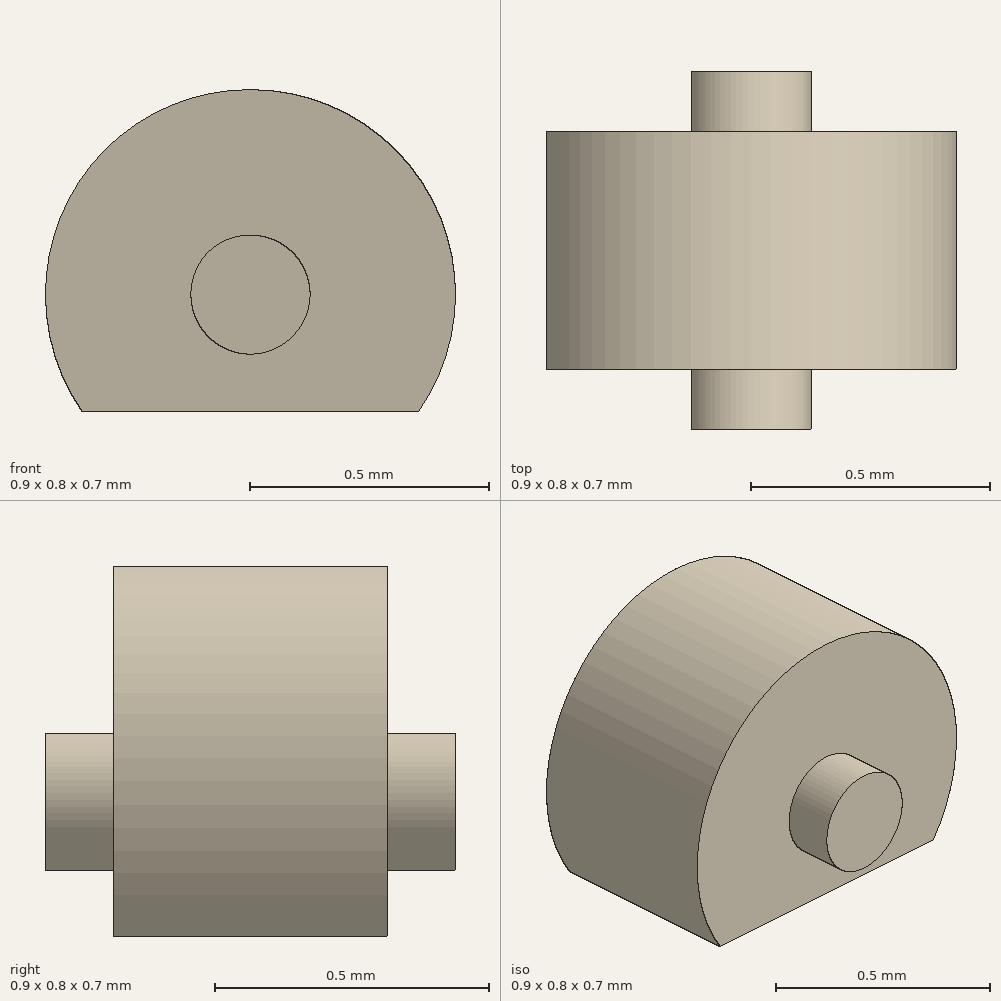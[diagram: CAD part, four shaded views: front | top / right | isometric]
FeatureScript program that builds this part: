
annotation { "Feature Type Name" : "Feature", "Feature Type Description" : "" }
export const myFeature = defineFeature(function(context is Context, id is Id, definition is map)
    precondition{}
    {
        {
            var Q0;
            Q0=qCreatedBy(makeId("Front.planeOp"),FACE);
            var sketch = newSketch(context, id + "F0", { "sketchPlane" : qUnion([Q0])});
            skCircle(sketch, "E0", {"center": v(0, 0) * mm, "radius": 0.43 * mm});
            skCircle(sketch, "E1", {"center": v(0, 0) * mm, "radius": 0.12 * mm});
            skLineSegment(sketch, "E2.bottom", {"start": v(-0.6, -0.24) * mm, "end": v(0.68, -0.24) * mm});
            skLineSegment(sketch, "E2.top", {"start": v(-0.6, -0.78) * mm, "end": v(0.68, -0.78) * mm});
            skLineSegment(sketch, "E2.left", {"start": v(-0.6, -0.24) * mm, "end": v(-0.6, -0.78) * mm});
            skLineSegment(sketch, "E2.right", {"start": v(0.68, -0.24) * mm, "end": v(0.68, -0.78) * mm});
            skSolve(sketch);
        }
        {
            var Q0;
            Q0=makeQuery(id+"F0.imprint","IMPRINT",FACE,{"disambiguationData":[TD([[makeQuery(id+"F0.imprint","IMPRINT",EDGE,{"derivedFrom":sQuery(id+"F0.wireOp",EDGE,"E1")}),-1.0]])]});
            extrude(context, id + "F1", {"entities" : qUnion([Q0]), "depth" : 0.5 * mm, "offsetDistance" : 25 * mm});
        }
        {
            var Q0;
            Q0=makeQuery(id+"F1.opExtrude","SWEPT_FACE",FACE,{"disambiguationData":[OSD([sQuery(id+"F0.wireOp",EDGE,"E2.bottom")])]});
            var sketch = newSketch(context, id + "F2", { "sketchPlane" : qUnion([Q0])});
            skCircle(sketch, "E3", {"center": v(0, 0.25) * mm, "radius": 0.12 * mm});
            skSolve(sketch);
        }
        {
            var Q0;
            Q0=makeQuery(id+"F0.imprint","IMPRINT",FACE,{"disambiguationData":[TD([[makeQuery(id+"F0.imprint","IMPRINT",EDGE,{"derivedFrom":sQuery(id+"F0.wireOp",EDGE,"E1")}),1.0]])]});
            extrude(context, id + "F3", {"entities" : qUnion([Q0]), "operationType" : NewBodyOperationType.ADD, "depth" : 0.62 * mm, "offsetDistance" : 25 * mm, "hasSecondDirection" : true, "secondDirectionOppositeDirection" : true, "secondDirectionDepth" : 0.12 * mm});
        }
        {
            var Q0;
            Q0=makeQuery(id+"F2.imprint","IMPRINT",FACE,{"disambiguationData":[TD([[makeQuery(id+"F2.imprint","IMPRINT",EDGE,{"derivedFrom":sQuery(id+"F2.wireOp",EDGE,"E3")}),1.0]])]});
            extrude(context, id + "F4", {"entities" : qUnion([Q0]), "operationType" : NewBodyOperationType.REMOVE, "oppositeDirection" : true, "depth" : 0.5 * mm, "offsetDistance" : 25 * mm});
        }
    });
